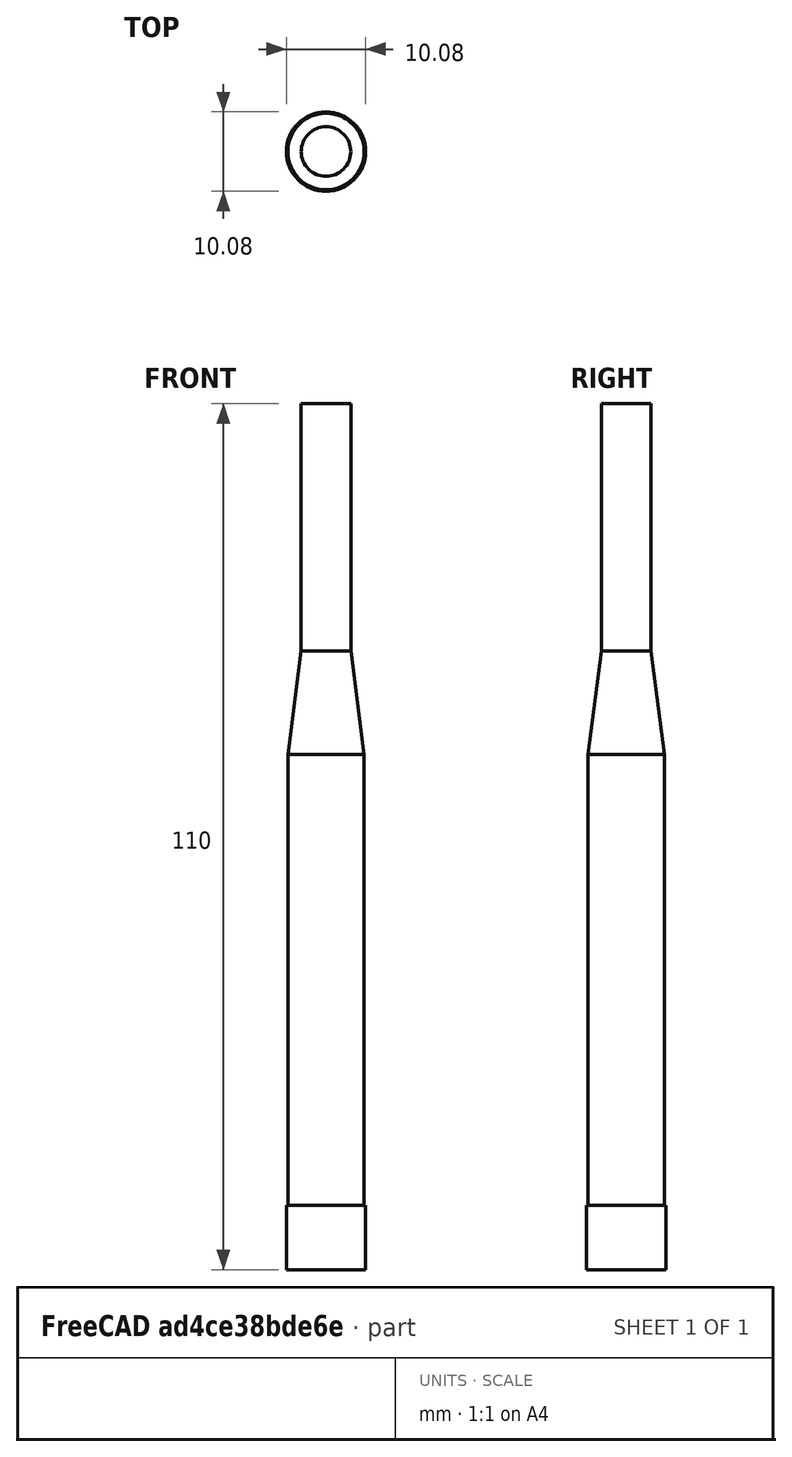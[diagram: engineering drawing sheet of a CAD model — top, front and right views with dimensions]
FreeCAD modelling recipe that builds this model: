
FCSTD DOCUMENT  (FreeCAD 1.0R39109 (Git))
Label: antenne
License: All rights reserved
LicenseURL: http://en.wikipedia.org/wiki/All_rights_reserved
objects: Sketcher::SketchObject×1, PartDesign::Revolution×1, PartDesign::Body×1, App::Part×1
note: 6 computed .brp shape members not serialized (recipe doc carries the construction recipe); baked Part::Feature solids carry a one-line shape summary decoded from their .brp

FEATURE [Sketcher::SketchObject] Sketch002
  ArcFitTolerance = 0
  AttachmentSupport = -> [YZ_Plane]
  FullyConstrained = true
  MakeInternals = false
  MapMode = 5
  Placement = pos=(0,0,0) rot=(0.57735,0.57735,0.57735;2.0944rad)
  sketch-geometry (19):
    g0: LineSegment StartX=-5.04 StartY=0 StartZ=0 EndX=0 EndY=0 EndZ=0
    g1: LineSegment [constr] StartX=5.04 StartY=2e-16 StartZ=0 EndX=5.04 EndY=8.18 EndZ=0
    g2: LineSegment [constr] StartX=5.04 StartY=8.18 StartZ=0 EndX=4.85 EndY=8.18 EndZ=0
    g3: LineSegment StartX=-5.04 StartY=8.18 StartZ=0 EndX=-5.04 EndY=0 EndZ=0
    g4: LineSegment [constr] StartX=-4.85 StartY=8.18 StartZ=0 EndX=4.85 EndY=8.18 EndZ=0
    g5: LineSegment [constr] StartX=4.85 StartY=8.18 StartZ=0 EndX=4.85 EndY=65.47 EndZ=0
    g6: LineSegment [constr] StartX=4.85 StartY=65.47 StartZ=0 EndX=3.15 EndY=78.6 EndZ=0
    g7: LineSegment StartX=-4.85 StartY=65.47 StartZ=0 EndX=-4.85 EndY=8.18 EndZ=0
    g8: LineSegment StartX=-3.15 StartY=110 StartZ=0 EndX=0 EndY=110 EndZ=0
    g9: LineSegment [constr] StartX=3.15 StartY=110 StartZ=0 EndX=3.15 EndY=78.6 EndZ=0
    g10: LineSegment [constr] StartX=3.15 StartY=78.6 StartZ=0 EndX=-3.15 EndY=78.6 EndZ=0
    g11: LineSegment StartX=-3.15 StartY=78.6 StartZ=0 EndX=-3.15 EndY=110 EndZ=0
    g12: LineSegment StartX=-3.15 StartY=78.6 StartZ=0 EndX=-4.85 EndY=65.47 EndZ=0
    g13: LineSegment StartX=-4.85 StartY=8.18 StartZ=0 EndX=-5.04 EndY=8.18 EndZ=0
    g14: LineSegment [constr] StartX=-4.85 StartY=65.47 StartZ=0 EndX=4.85 EndY=65.47 EndZ=0
    g15: GeomPoint [constr] X=0 Y=8.18 Z=0
    g16: GeomPoint [constr] X=0 Y=78.6 Z=0
    g17: LineSegment StartX=0 StartY=110 StartZ=0 EndX=0 EndY=0 EndZ=0
    g18: LineSegment [constr] StartX=0 StartY=0 StartZ=0 EndX=5.04 EndY=2e-16 EndZ=0
  constraints (47):
    c: Coincident(g1,g2)
    c: Coincident(g13,g3)
    c: Coincident(g3,g0)
    c: Horizontal(g0)
    c: Horizontal(g2)
    c: Vertical(g1)
    c: Vertical(g3)
    c: Coincident(g4,g5)
    c: Coincident(g5,g6)
    c: Coincident(g12,g7)
    c: Coincident(g7,g4)
    c: Horizontal(g4)
    c: Vertical(g5)
    c: Vertical(g7)
    c: Coincident(g9,g10)
    c: Coincident(g10,g11)
    c: Horizontal(g8)
    c: Horizontal(g10)
    c: Vertical(g9)
    c: Vertical(g11)
    c: Coincident(g6,g9)
    c: Coincident(g10,g12)
    c: Coincident(g13,g4)
    c: Horizontal(g13)
    c: DistanceX(g8,g9) = 6.3
    c: DistanceY(g1,g6) = 78.6
    c: Coincident(g14,g7)
    c: Coincident(g14,g5)
    c: Horizontal(g14)
    c: Coincident(g5,g2)
    c: DistanceY(g1,g9) = 110
    c: PointOnObject(g15,g-2)
    c: Symmetric(g2,g7,g15)
    c: PointOnObject(g16,g-2)
    c: Symmetric(g11,g6,g16)
    c: DistanceX(g7,g2) = 9.7
    c: DistanceY(g3,g3) = 8.18
    c: DistanceX(g0,g1) = 10.08
    c: Coincident(g17,g-1)
    c: Coincident(g17,g8)
    c: Symmetric(g8,g9,g8)
    c: Coincident(g11,g8)
    c: Coincident(g18,g0)
    c: Coincident(g18,g1)
    c: Coincident(g17,g0)
    c: Symmetric(g0,g1,g0)
    c: DistanceY(g0,g7) = 65.47
FEATURE [PartDesign::Revolution] Revolution
  Angle = 360
  Angle2 = 60
  Axis = (0,0,1)
  Base = (0,0,0)
  Placement = pos=(0,0,0) rot=(1,1,1;2.0944rad)
  Profile = -> Sketch002
  ReferenceAxis = -> Sketch002 [V_Axis]
  Suppressed = false
  Type = 0
FEATURE [PartDesign::Body] Body  label="Corps"
  AllowCompound = false
  Group = -> [Sketch002,Revolution]
  Origin = -> Origin
  Tip = -> Revolution
FEATURE [App::Part] Part
  Group = -> [Body]
  Origin = -> Origin001
